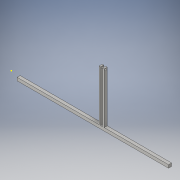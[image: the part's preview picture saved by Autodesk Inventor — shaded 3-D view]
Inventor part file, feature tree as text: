
AUTODESK INVENTOR PART (.ipt)
format: ipt  version: 2016 (Build 200138000, 138)  size: 131,584 bytes
history: native  units: in
note: dims shown in document units (in); Inventor stores cm internally (conversion verified against a paired STEP export)
features: thicken_offset x6, sketch x3, extrude x2, hole x1
ambient origin geometry x8: Origin, YZ Plane, XZ Plane, XY Plane, X Axis, Y Axis, Z Axis, Center Point
bodies: Solid1 (feature_tree)
feature tree (12):
  extrude  "Extrusion1"  Depth=0.25in
  extrude  "Extrusion3"  Depth=0.125in
  hole  "Hole2"  [1 undecoded]
  sketch  "Sketch4"  dims[d18=0.125in d19=4.191in d20=0.0in d21=0.125in d22=0.125in d23=0.125in d24=0.75in d25=0.375in d26=0.25in d27=0.5635in d28=1.0in d29=0.8108in d30=1.059in d31=1.059in d32=1.316in d33=1.316in d34=2.5in d35=2.5in d54=0.5in d55=0.5in d56=0.3in d57=0.3in d58=0.3in d59=0.3in]
  thicken_offset  "Thicken1"
  thicken_offset  "Thicken2"
  thicken_offset  "Thicken3"
  thicken_offset  "Thicken4"
  thicken_offset  "Thicken5"
  thicken_offset  "Thicken6"
  sketch  "Sketch1"  dims[d0=11.25in d1=0.25in]
  sketch  "Sketch3"  dims[d2=0.25in d3=0.0in d17=0.125in]
note: 1 required parameter value undecoded (feature->parameter linkage not recoverable at this tier; creation-order binding heuristic only, values carry confidence <= 0.55)
